FCSTD DOCUMENT  (FreeCAD 0.21R33771 (Git))
Label: circlesTemplate
License: All rights reserved
LicenseURL: http://en.wikipedia.org/wiki/All_rights_reserved
objects: Spreadsheet::Sheet×1, Sketcher::SketchObject×1, PartDesign::Body×1
note: 2 computed .brp shape members not serialized (recipe doc carries the construction recipe); baked Part::Feature solids carry a one-line shape summary decoded from their .brp

FEATURE [Spreadsheet::Sheet] Spreadsheet  label="ss"
  cells = A1='name; B1='value; C1='desc; A2='diaLg; B2(diaLg)=20; A3='diaSm; B3(diaSm)=5; A4='offsetVert; B4(offsetVert)=25
FEATURE [Sketcher::SketchObject] Sketch
  FullyConstrained = false
  MapMode = 5
  Support = -> [XY_Plane]
  expr: Constraints[0] = <<ss>>.diaLg
  expr: Constraints[1] = <<ss>>.offsetVert
  expr: Constraints[3] = <<ss>>.diaSm
  expr: Constraints[4] = <<ss>>.offsetVert + <<ss>>.diaLg / 2
  sketch-geometry (2):
    g0: Circle CenterX=0 CenterY=25 CenterZ=0 NormalX=0 NormalY=0 NormalZ=1 AngleXU=0 Radius=10
    g1: Circle CenterX=0 CenterY=35 CenterZ=0 NormalX=0 NormalY=0 NormalZ=1 AngleXU=0 Radius=2.5
  constraints (5):
    c: Diameter(g0) = 20
    c: DistanceY(g-1,g0) = 25
    c: PointOnObject(g1,g-2)
    c: Diameter(g1) = 5
    c: Distance(g1,g-1) = 35
FEATURE [PartDesign::Body] Body
  Group = -> [Sketch]
  Origin = -> Origin
